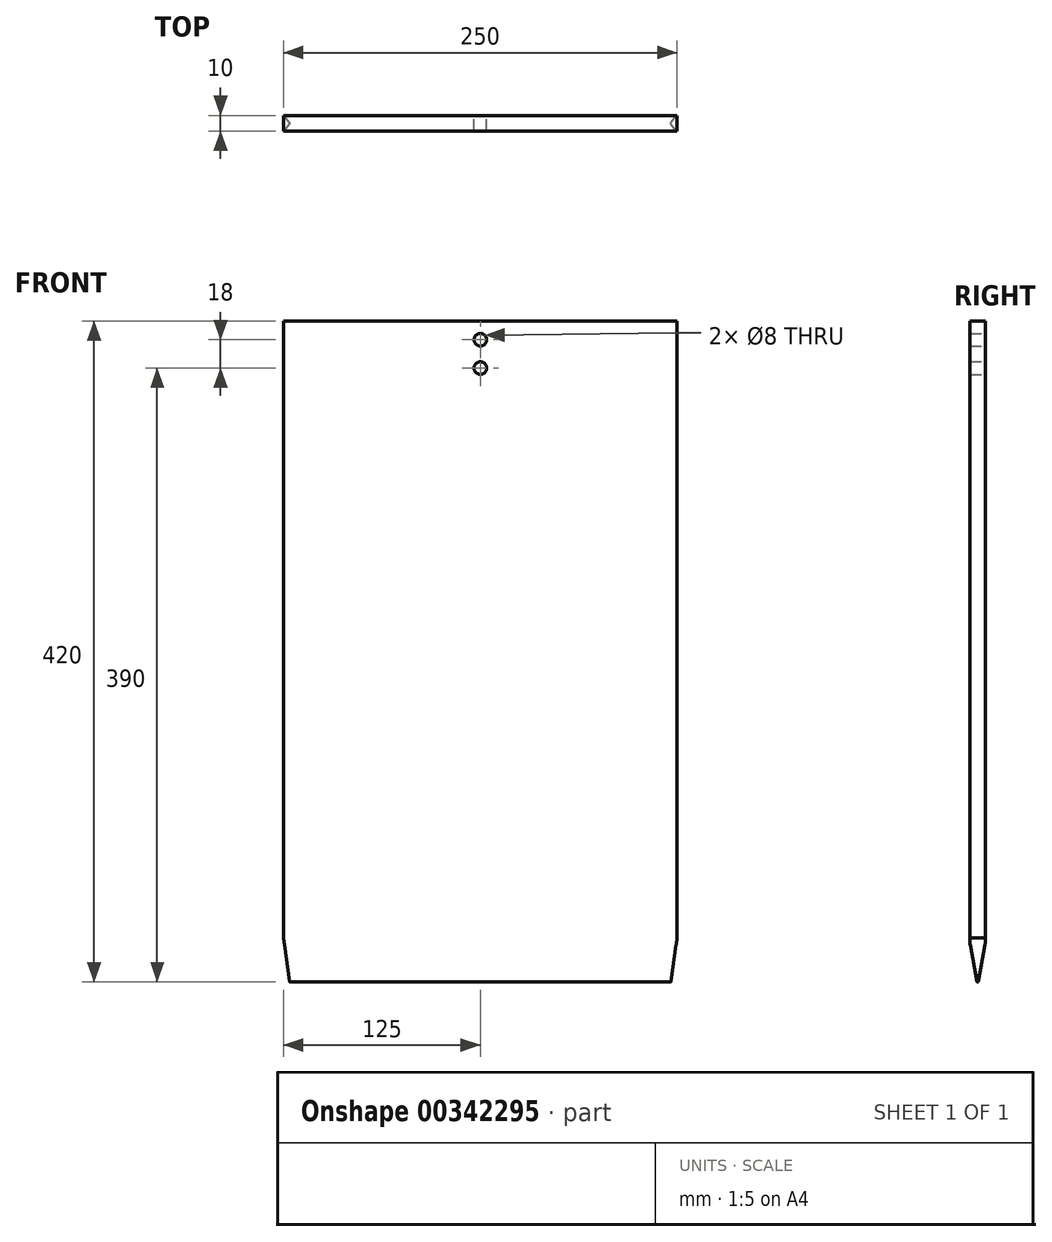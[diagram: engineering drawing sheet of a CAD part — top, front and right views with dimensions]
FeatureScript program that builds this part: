
annotation { "Feature Type Name" : "Feature", "Feature Type Description" : "" }
export const myFeature = defineFeature(function(context is Context, id is Id, definition is map)
    precondition{}
    {
        {
            var Q0;
            Q0=qCreatedBy(makeId("Right.planeOp"),FACE);
            var sketch = newSketch(context, id + "F0", { "sketchPlane" : qUnion([Q0])});
            skLineSegment(sketch, "E0.bottom", {"start": v(5, 210) * mm, "end": v(-5, 210) * mm});
            skLineSegment(sketch, "E0.top", {"start": v(5, -210) * mm, "end": v(-5, -210) * mm});
            skLineSegment(sketch, "E0.left", {"start": v(5, 210) * mm, "end": v(5, -182.83) * mm});
            skLineSegment(sketch, "E0.right", {"start": v(-5, 210) * mm, "end": v(-5, -182.83) * mm});
            skPoint(sketch, "E0.middle", {"position": v(0, 0) * mm});
            skPoint(sketch, "E1", {"position": v(0, -210) * mm});
            skCircle(sketch, "E2", {"center": v(0, -209.5) * mm, "radius": 0.5 * mm});
            skLineSegment(sketch, "E3", {"start": v(-4.67, -186.38) * mm, "end": v(-0.5, -209.59) * mm});
            skLineSegment(sketch, "E4", {"start": v(0.5, -209.59) * mm, "end": v(4.69, -186.4) * mm});
            skPoint(sketch, "E5.newPointB", {"position": v(-6.67, -175.28) * mm});
            skArc(sketch, "E5.filletArc", {"start": v(-5, -182.83) * mm, "mid": v(-4.91, -184.61) * mm, "end": v(-4.67, -186.38) * mm});
            skPoint(sketch, "E6.newPointA", {"position": v(5, -282.92) * mm});
            skPoint(sketch, "E6.newPointB", {"position": v(6.7, -175.28) * mm});
            skArc(sketch, "E6.filletArc", {"start": v(4.69, -186.4) * mm, "mid": v(4.93, -184.62) * mm, "end": v(5, -182.83) * mm});
            skSolve(sketch);
        }
        {
            var Q0;
            {var subQ4=sQuery(id+"F0.wireOp",EDGE,"E0.bottom");Q0=makeQuery(id+"F0.imprint","IMPRINT",FACE,{"disambiguationData":[TD([[makeQuery(id+"F0.imprint","IMPRINT",EDGE,{"derivedFrom":subQ4}),1.0]])]});}
            var Q1;
            {var subQ0=sQuery(id+"F0.wireOp",EDGE,"E2");var subQ1=makeQuery(id+"F0.imprint","INTERSECT",VERTEX,{"derivedFrom":[subQ0,sQuery(id+"F0.wireOp",EDGE,"E3")]});Q1=makeQuery(id+"F0.imprint","IMPRINT",FACE,{"disambiguationData":[TD([[makeQuery(id+"F0.imprint","IMPRINT",EDGE,{"disambiguationData":[TD([[subQ1,-1.0]])],"derivedFrom":subQ0}),1.0]])]});}
            extrude(context, id + "F1", {"entities" : qUnion([Q0, Q1]), "endBound" : BoundingType.SYMMETRIC, "depth" : 250 * mm, "offsetDistance" : 25 * mm});
        }
        {
            var Q0;
            Q0=makeQuery(id+"F1.opExtrude","SWEPT_FACE",FACE,{"disambiguationData":[OSD([sQuery(id+"F0.wireOp",EDGE,"E0.left")])]});
            var sketch = newSketch(context, id + "F2", { "sketchPlane" : qUnion([Q0])});
            skLineSegment(sketch, "E7", {"start": v(-125, -182) * mm, "end": v(-121, -210) * mm});
            skLineSegment(sketch, "E8", {"start": v(-125.1, -210) * mm, "end": v(-121, -210) * mm});
            skLineSegment(sketch, "E9", {"start": v(-125, -182) * mm, "end": v(-125.1, -210) * mm});
            skLineSegment(sketch, "E10.MirrorCS", {"start": v(125, -182) * mm, "end": v(121, -210) * mm});
            skLineSegment(sketch, "E11.MirrorCS", {"start": v(125, -182) * mm, "end": v(125.1, -210) * mm});
            skLineSegment(sketch, "E12.MirrorCS", {"start": v(125.1, -210) * mm, "end": v(121, -210) * mm});
            skCircle(sketch, "E13", {"center": v(0, 198) * mm, "radius": 4 * mm});
            skCircle(sketch, "E14", {"center": v(0, 180) * mm, "radius": 4 * mm});
            skSolve(sketch);
        }
        {
            var Q0;
            Q0=qSketchRegion(id+"F2",true);
            extrude(context, id + "F3", {"entities" : qUnion([Q0]), "operationType" : NewBodyOperationType.REMOVE, "oppositeDirection" : true, "depth" : 25 * mm});
        }
    });
